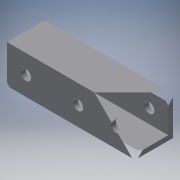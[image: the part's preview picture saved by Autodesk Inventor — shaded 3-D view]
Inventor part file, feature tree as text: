
AUTODESK INVENTOR PART (.ipt)
format: ipt  version: 2016 (Build 200138000, 138)  size: 115,200 bytes
history: native  units: in
note: dims shown in document units (in); Inventor stores cm internally (conversion verified against a paired STEP export)
features: extrude x2, sketch x2
ambient origin geometry x8: Origin, YZ Plane, XZ Plane, XY Plane, X Axis, Y Axis, Z Axis, Center Point
bodies: Solid1 (feature_tree)
feature tree (4):
  extrude  "Extrusion1"  Depth=1.0in
  extrude  "Extrusion2"  Depth=3.375in TaperAngle=0.0deg
  sketch  "Sketch1"  dims[d0=1.0in d1=1.0in]
  sketch  "Sketch2"  dims[d2=0.125in d3=3.375in d4=0.0in d5=0.2656in d6=0.2656in d7=0.5in d8=0.5in d9=0.5in d10=0.5in d11=1.0in d12=0.0in d13=0.2656in d15=0.5in d16=1.0in]
